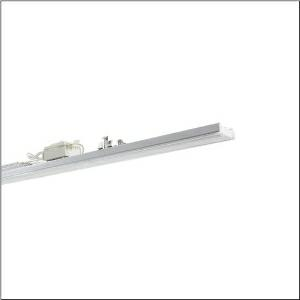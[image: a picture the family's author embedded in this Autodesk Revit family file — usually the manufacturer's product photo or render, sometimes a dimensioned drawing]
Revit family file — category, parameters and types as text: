
# Revit family: licross_11_recessed_mo_51tl12dne9xg
name_source: partatom
category: Lighting Fixtures
units: mm (PartAtom-declared; Revit-internal decimal feet)

## family parameters
Cut with Voids When Loaded = No
Host = Face
Light Source = No
Part Type = Normal
Room Calculation Point = No
Round Connector Dimension = Use Diameter
Shared = No

## types (1)
- --- (1 x LED, 9450 lm, 56.2 W, 5000K)
    Apparent Load = 56 VA
    CIE Flux Codes = 67 92 99 100 100
    Color Rendering = 90
    Color Temperature = 5000K
    Default Elevation = 1800 mm
    Description = Licross 11 Recessed MO, luminaire insert, of sheet steel, coil coated, white, length: 1.500mm, width: 66mm, height: 67mm, LED rated luminous flux: 9.450lm, light colour: 950, SDCM (Standard Deviation of Colour Matching)MacAdam ≤ 2 SDCM (initial), control gear: DALI 2, with plug, 5-pole, with phase selection, mains connection: 220..240V, AC, 50/60Hz, rated input power: 56W, internal wiring halogen-free, primary optical cover: cover, of PMMA, light emission: direct distribution, primary light characteristic: symmetric, protection rating (complete): IP40, insulation class (complete): insulation class I (protective earthing), certification: CE, ENEC, VDE, UKCA, protection symbol: D if used in an environment without relevant dust loads with corresponding accessories, impact resistance: IK06, permissible ambient temperature for indoor applications: -25..+35°C, corresponds to IFS (International Featured Standards) requirements for safety and quality in the food industry, reducing of maximum allowable ambient temperature of 5°C with ceiling mounting, LABS conformity tested according to VDMA 24364:2018-05, The light source and the operating device comply with the requirements of the Ecodesign Regulation (EU) 2019/2020 and are replaceable in accordance with this regulation, packaging unit: 1 piece
    Height = 58 mm
    Lamp = 1 x LED
    Lamp Light Flux = 9450 lm
    Lamp Power = 56.2 W
    Lamp count = 1
    Length = 1500 mm
    Luminous efficacy = 168 lm/W
    Manufacturer = Siteco
    ModVariant = No
    Model = 51TL12DNE9XG
    Mounting Place = Ceiling
    Mounting Type = Pendant
    Number of Poles = 1
    OnlyDefault = Yes
    Power Factor = 1
    Product Name = Licross 11 Recessed MO
    Product group = luminaire insert | ceiling pendant
    ProductGroupID = 901
    Protection Class = Protection class I
    Protection Degree = IP 40
    RLX_Detail_Level = 1
    RLX_Emergency_Light_Flux = 0 lm
    RLX_Emergency_Type = 0
    RLX_Emergency_Type_DB = No
    RlxData = <blob elided: 24765 chars, md5=1c513a5e>
    Socket = socket
    Standby Power = 0 W
    System Light Flux = 9450 lm
    System Power = 56 W
    Type Comments = factory setting: luminous flux: 100 % | dim-lin: 254 | 378 mA
    Type Image = l_1296930.jpg
    URL = http://relux.com
    VarID = @adj_056031
    Voltage = 0 V
    Weight = 0.00 kg
    Width = 66 mm

## geometry (parser evidence)
native form markers: Blend x4, Sweep x11
no freeform markers — native parametric forms only
